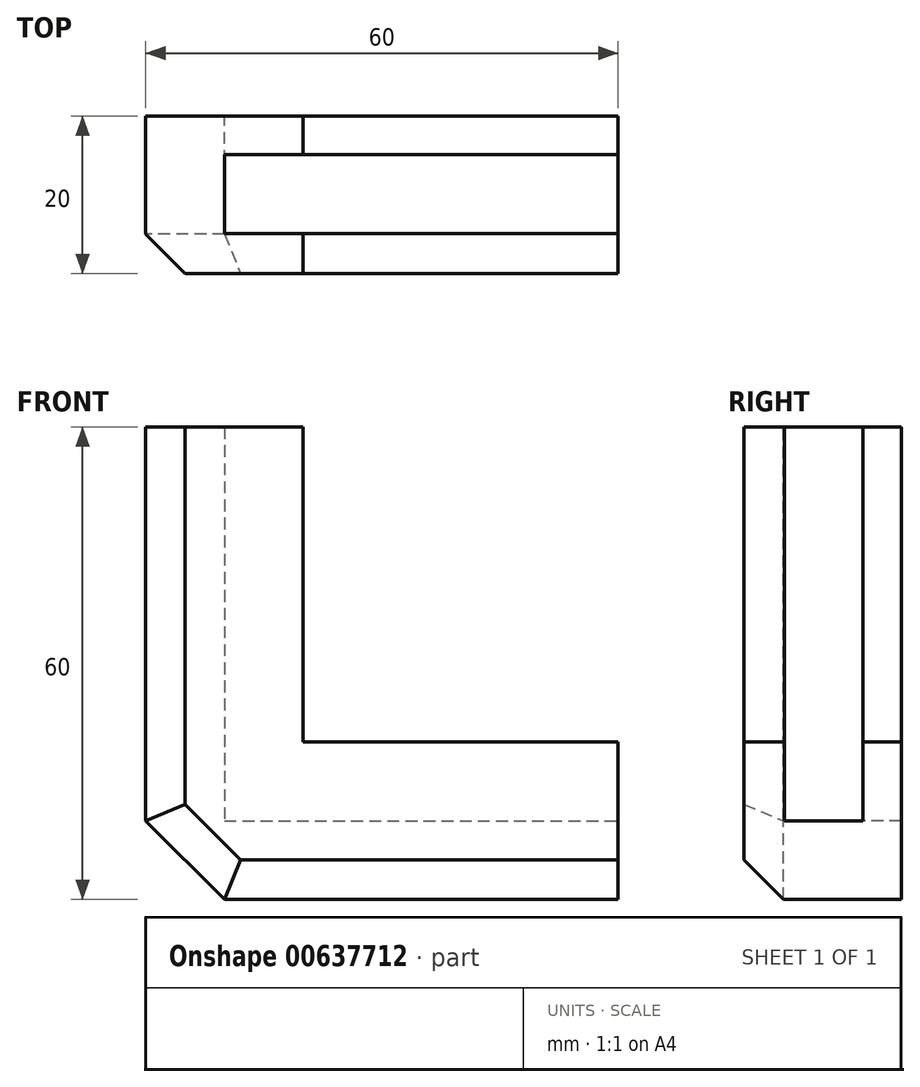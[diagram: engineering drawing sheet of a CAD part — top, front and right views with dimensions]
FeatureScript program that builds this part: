
annotation { "Feature Type Name" : "Feature", "Feature Type Description" : "" }
export const myFeature = defineFeature(function(context is Context, id is Id, definition is map)
    precondition{}
    {
        {
            var Q0;
            Q0=qCreatedBy(makeId("Top.planeOp"),FACE);
            var sketch = newSketch(context, id + "F0", { "sketchPlane" : qUnion([Q0])});
            skLineSegment(sketch, "E0.bottom", {"start": v(0, 0) * mm, "end": v(60, 0) * mm});
            skLineSegment(sketch, "E0.top", {"start": v(0, 20) * mm, "end": v(60, 20) * mm});
            skLineSegment(sketch, "E0.left", {"start": v(0, 0) * mm, "end": v(0, 20) * mm});
            skLineSegment(sketch, "E0.right", {"start": v(60, 0) * mm, "end": v(60, 20) * mm});
            skSolve(sketch);
        }
        {
            var Q0;
            Q0=makeQuery(id+"F0.imprint","IMPRINT",FACE,{"disambiguationData":[TD([[makeQuery(id+"F0.imprint","IMPRINT",EDGE,{"derivedFrom":sQuery(id+"F0.wireOp",EDGE,"E0.bottom")}),1.0]])]});
            extrude(context, id + "F1", {"entities" : qUnion([Q0]), "depth" : 20 * mm, "offsetDistance" : 25 * mm});
        }
        {
            var Q0;
            Q0=qCreatedBy(makeId("Front.planeOp"),FACE);
            var sketch = newSketch(context, id + "F2", { "sketchPlane" : qUnion([Q0])});
            skLineSegment(sketch, "E1.bottom", {"start": v(0, 0) * mm, "end": v(20, 0) * mm});
            skLineSegment(sketch, "E1.top", {"start": v(0, 60) * mm, "end": v(20, 60) * mm});
            skLineSegment(sketch, "E1.left", {"start": v(0, 0) * mm, "end": v(0, 60) * mm});
            skLineSegment(sketch, "E1.right", {"start": v(20, 0) * mm, "end": v(20, 60) * mm});
            skSolve(sketch);
        }
        {
            var Q0;
            Q0=makeQuery(id+"F2.imprint","IMPRINT",FACE,{"disambiguationData":[TD([[makeQuery(id+"F2.imprint","IMPRINT",EDGE,{"derivedFrom":sQuery(id+"F2.wireOp",EDGE,"E1.bottom")}),1.0]])]});
            extrude(context, id + "F3", {"entities" : qUnion([Q0]), "operationType" : NewBodyOperationType.ADD, "oppositeDirection" : true, "depth" : 20 * mm, "offsetDistance" : 25 * mm});
        }
        {
            var Q0;
            Q0=makeQuery(id+"F3.opExtrude","SWEPT_FACE",FACE,{"disambiguationData":[OSD([sQuery(id+"F2.wireOp",EDGE,"E1.right")])]});
            var sketch = newSketch(context, id + "F4", { "sketchPlane" : qUnion([Q0])});
            skLineSegment(sketch, "E2.bottom", {"start": v(5.1, 60.95) * mm, "end": v(15.1, 60.95) * mm});
            skLineSegment(sketch, "E2.top", {"start": v(5.1, 4.95) * mm, "end": v(15.1, 4.95) * mm});
            skLineSegment(sketch, "E2.left", {"start": v(5.1, 60.95) * mm, "end": v(5.1, 4.95) * mm});
            skLineSegment(sketch, "E2.right", {"start": v(15.1, 60.95) * mm, "end": v(15.1, 4.95) * mm});
            skSolve(sketch);
        }
        {
            var Q0;
            {var subQ0=sQuery(id+"F4.wireOp",EDGE,"E2.left");var subQ1=sQuery(id+"F2.wireOp",EDGE,"E1.right");var subQ2=makeQuery(id+"F3.opExtrude","SWEPT_EDGE",EDGE,{"disambiguationData":[OSD([sQuery(id+"F2.wireOp",EDGE,"E1.top"),subQ1])]});var subQ3=makeQuery(id+"F4.imprint","INTERSECT",VERTEX,{"derivedFrom":[subQ2,subQ0]});Q0=makeQuery(id+"F4.imprint","IMPRINT",FACE,{"disambiguationData":[TD([[makeQuery(id+"F4.imprint","IMPRINT",EDGE,{"disambiguationData":[TD([[subQ3,1.0]])],"derivedFrom":subQ2}),1.0]])]});}
            extrude(context, id + "F5", {"entities" : qUnion([Q0]), "operationType" : NewBodyOperationType.REMOVE, "oppositeDirection" : true, "depth" : 10 * mm, "offsetDistance" : 25 * mm});
        }
        {
            var Q0;
            {var subQ0=sQuery(id+"F0.wireOp",EDGE,"E0.right");var subQ1=sQuery(id+"F0.wireOp",EDGE,"E0.left");var subQ2=sQuery(id+"F0.wireOp",EDGE,"E0.top");var subQ3=sQuery(id+"F0.wireOp",EDGE,"E0.bottom");Q0=makeQuery(id+"F5.boolean.opBoolean","MERGE",FACE,{"derivedFrom":[makeQuery(id+"F1.opExtrude","CAP_FACE",FACE,{"disambiguationData":[OSD([subQ3,subQ2,subQ1,subQ0])],"isStart":false}),makeQuery(id+"F5.opExtrude","SWEPT_FACE",FACE,{"disambiguationData":[OSD([subQ3,subQ2,subQ1,subQ0,sQuery(id+"F2.wireOp",EDGE,"E1.right")])]})]});}
            var sketch = newSketch(context, id + "F6", { "sketchPlane" : qUnion([Q0])});
            skLineSegment(sketch, "E3.bottom", {"start": v(10, 15.1) * mm, "end": v(60, 15.1) * mm});
            skLineSegment(sketch, "E3.top", {"start": v(10, 5.1) * mm, "end": v(60, 5.1) * mm});
            skLineSegment(sketch, "E3.left", {"start": v(10, 15.1) * mm, "end": v(10, 5.1) * mm});
            skLineSegment(sketch, "E3.right", {"start": v(60, 15.1) * mm, "end": v(60, 5.1) * mm});
            skSolve(sketch);
        }
        {
            var Q0;
            {var subQ14=sQuery(id+"F6.wireOp",EDGE,"E3.left");Q0=makeQuery(id+"F6.imprint","IMPRINT",FACE,{"disambiguationData":[TD([[makeQuery(id+"F6.imprint","IMPRINT",EDGE,{"derivedFrom":subQ14}),-1.0]])]});}
            extrude(context, id + "F7", {"entities" : qUnion([Q0]), "operationType" : NewBodyOperationType.REMOVE, "oppositeDirection" : true, "depth" : 10 * mm, "offsetDistance" : 25 * mm});
        }
        {
            var Q0;
            Q0=makeQuery(id+"F1.opExtrude","CAP_EDGE",EDGE,{"disambiguationData":[OSD([sQuery(id+"F0.wireOp",EDGE,"E0.left")])],"isStart":true});
            chamfer(context, id + "F8", {"entities" : qUnion([Q0]), "width" : 10 * mm, "tangentPropagation" : true});
        }
        {
            var Q0;
            Q0=makeQuery(id+"F1.opExtrude","CAP_EDGE",EDGE,{"disambiguationData":[OSD([sQuery(id+"F0.wireOp",EDGE,"E0.bottom")])],"isStart":true});
            var Q1;
            Q1=makeQuery(id+"F8.opChamfer","BLEND_EDGE",EDGE,{"blendedFrom":[makeQuery(id+"F1.opExtrude","CAP_EDGE",EDGE,{"disambiguationData":[OSD([sQuery(id+"F0.wireOp",EDGE,"E0.left")])],"isStart":true}),makeQuery(id+"F3.boolean.opBoolean","MERGE",FACE,{"derivedFrom":[makeQuery(id+"F1.opExtrude","SWEPT_FACE",FACE,{"disambiguationData":[OSD([sQuery(id+"F0.wireOp",EDGE,"E0.bottom")])]}),makeQuery(id+"F3.opExtrude","CAP_FACE",FACE,{"disambiguationData":[OSD([sQuery(id+"F2.wireOp",EDGE,"E1.bottom"),sQuery(id+"F2.wireOp",EDGE,"E1.top"),sQuery(id+"F2.wireOp",EDGE,"E1.left"),sQuery(id+"F2.wireOp",EDGE,"E1.right")])],"isStart":true})]})],"blendedInto":[makeQuery(id+"F3.boolean.opBoolean","MERGE",FACE,{"derivedFrom":[makeQuery(id+"F1.opExtrude","SWEPT_FACE",FACE,{"disambiguationData":[OSD([sQuery(id+"F0.wireOp",EDGE,"E0.bottom")])]}),makeQuery(id+"F3.opExtrude","CAP_FACE",FACE,{"disambiguationData":[OSD([sQuery(id+"F2.wireOp",EDGE,"E1.bottom"),sQuery(id+"F2.wireOp",EDGE,"E1.top"),sQuery(id+"F2.wireOp",EDGE,"E1.left"),sQuery(id+"F2.wireOp",EDGE,"E1.right")])],"isStart":true})]})]});
            chamfer(context, id + "F9", {"entities" : qUnion([Q0, Q1]), "width" : 5 * mm, "tangentPropagation" : true});
        }
        {
            var Q0;
            Q0=makeQuery(id+"F3.boolean.opBoolean","MERGE",EDGE,{"derivedFrom":[makeQuery(id+"F1.opExtrude","SWEPT_EDGE",EDGE,{"disambiguationData":[OSD([sQuery(id+"F0.wireOp",EDGE,"E0.bottom"),sQuery(id+"F0.wireOp",EDGE,"E0.left")])]}),makeQuery(id+"F3.opExtrude","CAP_EDGE",EDGE,{"disambiguationData":[OSD([sQuery(id+"F2.wireOp",EDGE,"E1.left")])],"isStart":true})]});
            chamfer(context, id + "F10", {"entities" : qUnion([Q0]), "width" : 5 * mm, "tangentPropagation" : true});
        }
    });
